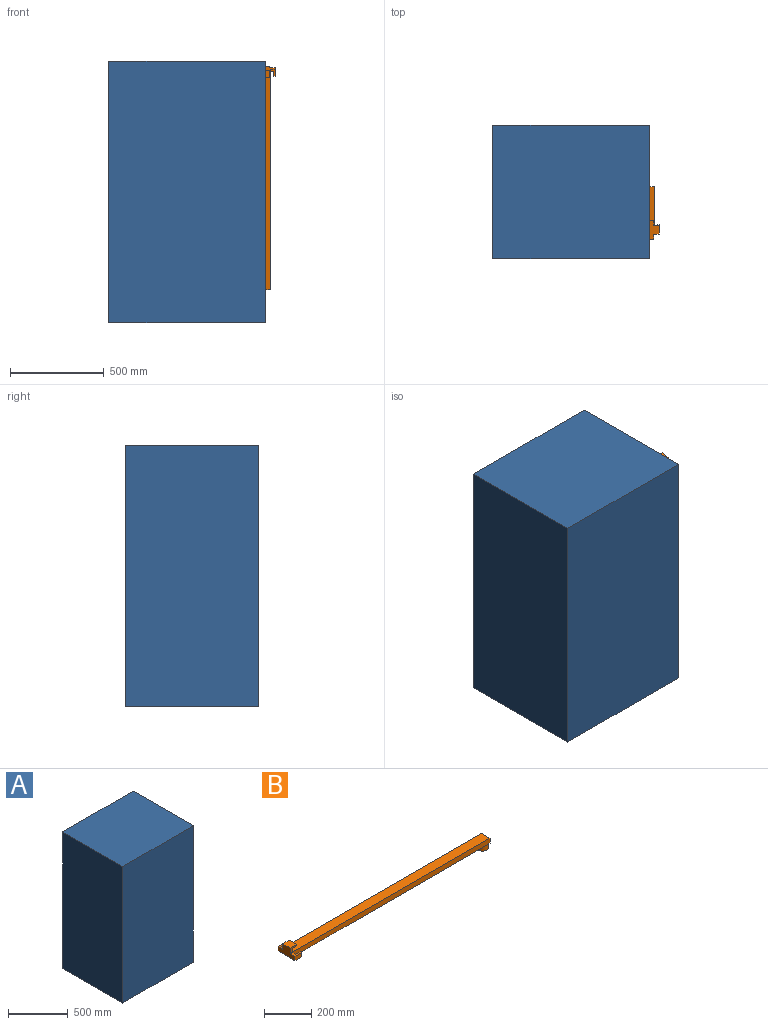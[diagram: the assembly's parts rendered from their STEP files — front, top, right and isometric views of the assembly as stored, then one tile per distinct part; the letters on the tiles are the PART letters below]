
ASSEMBLY  parts=2 mates=1
PART A: 8 faces, bbox 838.2x711.2x1397 mm
  f0: plane 1397x711.2mm, normal (1,0,0), area 991519.6mm2, adj f1,f3,f4,f5,f6
  f1: plane 1397x838.2mm, normal (0,1,0), area 1170965.4mm2, adj f0,f2,f4,f5
  f2: plane 1397x711.2mm, normal (-1,0,0), area 993546.4mm2, adj f1,f3,f4,f5
  f3: plane 1397x838.2mm, normal (0,-1,0), area 1170965.4mm2, adj f0,f2,f4,f5
  f4: plane 838.2x711.2mm, normal (0,0,1), area 596127.8mm2, adj f0,f1,f2,f3
  f5: plane 838.2x711.2mm, normal (0,0,-1), area 596127.8mm2, adj f0,f1,f2,f3
  f6: cylinder r=25.4mm len=50.8mm, axis (1,0,0), area 4053.7mm2, adj f0,f7
  f7: plane 50.8x50.8mm, normal (1,0,0), area 2026.8mm2, adj f6
PART B: 27 faces, bbox 1197.8x101.6x76.2 mm
  f0: plane 21.36x11.66mm, normal (0,0,-1), area 73.5mm2, adj f2,f8,f25
  f1: plane 21.36x11.66mm, normal (0,0,-1), area 73.5mm2, adj f7,f8,f25
  f2: plane 1193.8x25.4mm, normal (0,1,0), area 30040.3mm2, adj f0,f5,f6,f8,f9,f19,f20
  f3: plane 22.23x17.78mm, normal (1,0,0), area 395.2mm2, adj f7,f9,f15,f17
  f4: plane 44.45x17.78mm, normal (1,0,0), area 790.3mm2, adj f5,f10,f11,f13
  f5: plane 1193.8x50.8mm, normal (0,0,1), area 60080.5mm2, adj f2,f4,f6,f7,f8,f10,f11
  f6: plane 101.6x50.8mm, normal (-1,0,0), area 3548.4mm2, adj f2,f5,f7,f9,f10,f11,f12,f15
  f7: plane 1193.8x25.4mm, normal (0,-1,0), area 30040.3mm2, adj f1,f3,f5,f6,f8,f9,f15
  f8: plane 50.8x25.4mm, normal (1,0,0), area 1290.3mm2, adj f0,f1,f2,f5,f7,f24
  f9: plane 1172.44x101.6mm, normal (0,0,-1), area 59578.6mm2, adj f2,f3,f6,f7,f16,f17,f18,f20
  f10: plane 38.1x25.4mm, normal (0,-1,0), area 516.1mm2, adj f4,f5,f6,f12,f13,f14
  f11: plane 38.1x25.4mm, normal (0,1,0), area 516.1mm2, adj f4,f5,f6,f12,f13,f14
  f12: plane 44.45x38.1mm, normal (0,0,1), area 1693.5mm2, adj f6,f10,f11,f14
  f13: plane 44.45x25.4mm, normal (0,0,-1), area 1129mm2, adj f4,f10,f11,f14
  f14: plane 44.45x7.62mm, normal (1,0,0), area 338.7mm2, adj f10,f11,f12,f13
  f15: plane 38.1x25.4mm, normal (0,0,1), area 516.1mm2, adj f3,f6,f7,f16,f17,f18
  f16: plane 38.1x22.23mm, normal (0,-1,0), area 846.8mm2, adj f6,f9,f15,f18
  f17: plane 25.4x22.23mm, normal (0,1,0), area 564.5mm2, adj f3,f9,f15,f18
  f18: plane 22.23x7.62mm, normal (1,0,0), area 169.4mm2, adj f9,f15,f16,f17
  f19: plane 38.1x25.4mm, normal (0,0,1), area 516.1mm2, adj f2,f6,f20,f21,f22,f23
  f20: plane 22.23x17.78mm, normal (1,0,0), area 395.2mm2, adj f2,f9,f19,f22
  f21: plane 38.1x22.23mm, normal (0,1,0), area 846.8mm2, adj f6,f9,f19,f23
  f22: plane 25.4x22.23mm, normal (0,-1,0), area 564.5mm2, adj f9,f19,f20,f23
  f23: plane 22.23x7.62mm, normal (1,0,0), area 169.4mm2, adj f9,f19,f21,f22
  f24: plane 27.48x4.04mm, normal (0,0,1), area 75.2mm2, adj f8,f25
  f25: cylinder r=25.4mm len=50.8mm, axis (0,0,1), area 4053.7mm2, adj f0,f1,f9,f24,f26
  f26: plane 50.8x50.8mm, normal (0,0,-1), area 2026.8mm2, adj f25
PLACE A t=(282.68,107.28,380.01)mm fixed
PLACE B rot(axis=(0.09,0.99,0.09),90.4deg) t=(1076.97,379.3,629.02)mm
MATE revolute B.f25 <-> A.f6  axis (-1,0,0) through (1051.57,402.6,583.21)mm
